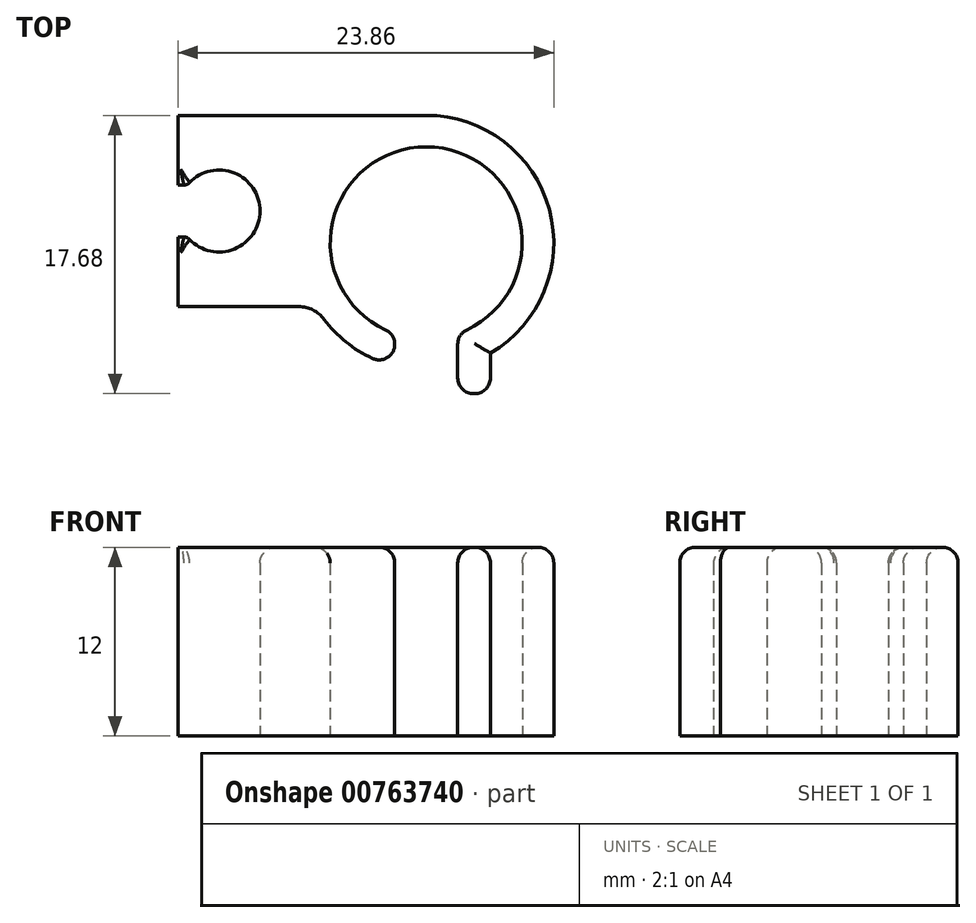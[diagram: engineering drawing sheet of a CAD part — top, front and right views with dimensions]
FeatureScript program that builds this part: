
annotation { "Feature Type Name" : "Feature", "Feature Type Description" : "" }
export const myFeature = defineFeature(function(context is Context, id is Id, definition is map)
    precondition{}
    {
        {
            var Q0;
            Q0=qCreatedBy(makeId("Top.planeOp"),FACE);
            var sketch = newSketch(context, id + "F0", { "sketchPlane" : qUnion([Q0])});
            skLineSegment(sketch, "E0", {"start": v(0, 34.7) * mm, "end": v(0, -47.17) * mm, "construction": true});
            skLineSegment(sketch, "E1", {"start": v(-51.33, 0) * mm, "end": v(61.47, 0) * mm, "construction": true});
            skArc(sketch, "E2", {"start": v(2.58, -5.53) * mm, "mid": v(0, 6.1) * mm, "end": v(-2.58, -5.53) * mm});
            skArc(sketch, "E3", {"start": v(4.08, -7) * mm, "mid": v(7.82, 2.11) * mm, "end": v(0, 8.1) * mm});
            skLineSegment(sketch, "E4", {"start": v(-8.1, 12.92) * mm, "end": v(-8.1, -12.54) * mm, "construction": true});
            skLineSegment(sketch, "E5", {"start": v(0, 8.1) * mm, "end": v(-15.76, 8.1) * mm});
            skLineSegment(sketch, "E6", {"start": v(-15.76, 8.1) * mm, "end": v(-15.76, 3.68) * mm});
            skLineSegment(sketch, "E7", {"start": v(-15.76, -4.05) * mm, "end": v(-8.09, -4.05) * mm});
            skLineSegment(sketch, "E8", {"start": v(-22.5, 2.03) * mm, "end": v(11.06, 2.03) * mm, "construction": true});
            skPoint(sketch, "E8.startSnap0", {"position": v(-15.76, 2.03) * mm});
            skArc(sketch, "E9", {"start": v(-15.03, 0.22) * mm, "mid": v(-10.56, 2.03) * mm, "end": v(-15.03, 3.83) * mm});
            skLineSegment(sketch, "E10", {"start": v(-15.4, 3.68) * mm, "end": v(-15.76, 3.68) * mm});
            skLineSegment(sketch, "E11.MirrorCS", {"start": v(-15.4, 0.38) * mm, "end": v(-15.76, 0.38) * mm});
            skLineSegment(sketch, "E12.trimOffspring", {"start": v(-15.76, 0.38) * mm, "end": v(-15.76, -4.05) * mm});
            skPoint(sketch, "E13.visualSharp", {"position": v(-15.17, 3.68) * mm});
            skArc(sketch, "E13.filletArc", {"start": v(-15.4, 3.68) * mm, "mid": v(-15.2, 3.72) * mm, "end": v(-15.03, 3.83) * mm});
            skPoint(sketch, "E14.visualSharp", {"position": v(-15.17, 0.38) * mm});
            skArc(sketch, "E14.filletArc", {"start": v(-15.03, 0.22) * mm, "mid": v(-15.2, 0.34) * mm, "end": v(-15.4, 0.38) * mm});
            skLineSegment(sketch, "E15", {"start": v(-2, -6.44) * mm, "end": v(-2, -6.44) * mm});
            skLineSegment(sketch, "E16.MirrorCS", {"start": v(2, -6.44) * mm, "end": v(2, -7.85) * mm});
            skLineSegment(sketch, "E17", {"start": v(3, -9.58) * mm, "end": v(3.08, -9.58) * mm});
            skLineSegment(sketch, "E18", {"start": v(4.08, -8.58) * mm, "end": v(4.08, -7) * mm});
            skLineSegment(sketch, "E19", {"start": v(2, -7.85) * mm, "end": v(2, -8.58) * mm});
            skPoint(sketch, "E20.visualSharp", {"position": v(2, -5.76) * mm});
            skArc(sketch, "E20.filletArc", {"start": v(2.58, -5.53) * mm, "mid": v(2.16, -5.9) * mm, "end": v(2, -6.44) * mm});
            skPoint(sketch, "E21.visualSharp", {"position": v(-2, -5.76) * mm});
            skArc(sketch, "E21.filletArc", {"start": v(-2, -6.44) * mm, "mid": v(-2.16, -5.9) * mm, "end": v(-2.58, -5.53) * mm});
            skPoint(sketch, "E22.visualSharp", {"position": v(-2, -7.85) * mm});
            skArc(sketch, "E22.filletArc", {"start": v(-3.42, -7.34) * mm, "mid": v(-2.46, -7.28) * mm, "end": v(-2, -6.44) * mm});
            skPoint(sketch, "E23.visualSharp", {"position": v(2, -9.58) * mm});
            skArc(sketch, "E23.filletArc", {"start": v(2, -8.58) * mm, "mid": v(2.3, -9.29) * mm, "end": v(3, -9.58) * mm});
            skPoint(sketch, "E24.visualSharp", {"position": v(4.08, -9.58) * mm});
            skArc(sketch, "E24.filletArc", {"start": v(3.08, -9.58) * mm, "mid": v(3.78, -9.29) * mm, "end": v(4.08, -8.58) * mm});
            skArc(sketch, "E25.trimOffspring", {"start": v(-6.49, -4.85) * mm, "mid": v(-5.1, -6.29) * mm, "end": v(-3.42, -7.34) * mm});
            skPoint(sketch, "E26.visualSharp", {"position": v(-7.02, -4.05) * mm});
            skArc(sketch, "E26.filletArc", {"start": v(-6.49, -4.85) * mm, "mid": v(-7.2, -4.26) * mm, "end": v(-8.09, -4.05) * mm});
            skSolve(sketch);
        }
        {
            var Q0;
            Q0 = qSketchRegion(id + "F0", true);
            extrude(context, id + "F1", {"entities" : qUnion([Q0]), "depth" : 12 * mm, "offsetDistance" : 25 * mm});
        }
        {
            var Q0;
            Q0=makeQuery(id+"F1.opExtrude","CAP_EDGE",EDGE,{"disambiguationData":[OSD([sQuery(id+"F0.wireOp",EDGE,"E9")])],"isStart":false});
            var Q1;
            Q1=makeQuery(id+"F1.opExtrude","CAP_EDGE",EDGE,{"disambiguationData":[OSD([sQuery(id+"F0.wireOp",EDGE,"E2")])],"isStart":false});
            var Q2;
            Q2=makeQuery(id+"F1.opExtrude","CAP_EDGE",EDGE,{"disambiguationData":[OSD([sQuery(id+"F0.wireOp",EDGE,"E5")])],"isStart":false});
            var Q3;
            Q3=makeQuery(id+"F1.opExtrude","CAP_EDGE",EDGE,{"disambiguationData":[OSD([sQuery(id+"F0.wireOp",EDGE,"E3")])],"isStart":false});
            fillet(context, id + "F2", {"entities" : qUnion([Q0, Q1, Q2, Q3]), "radius" : 1 * mm, "tangentPropagation" : true, "allowEdgeOverflow" : false});
        }
    });
